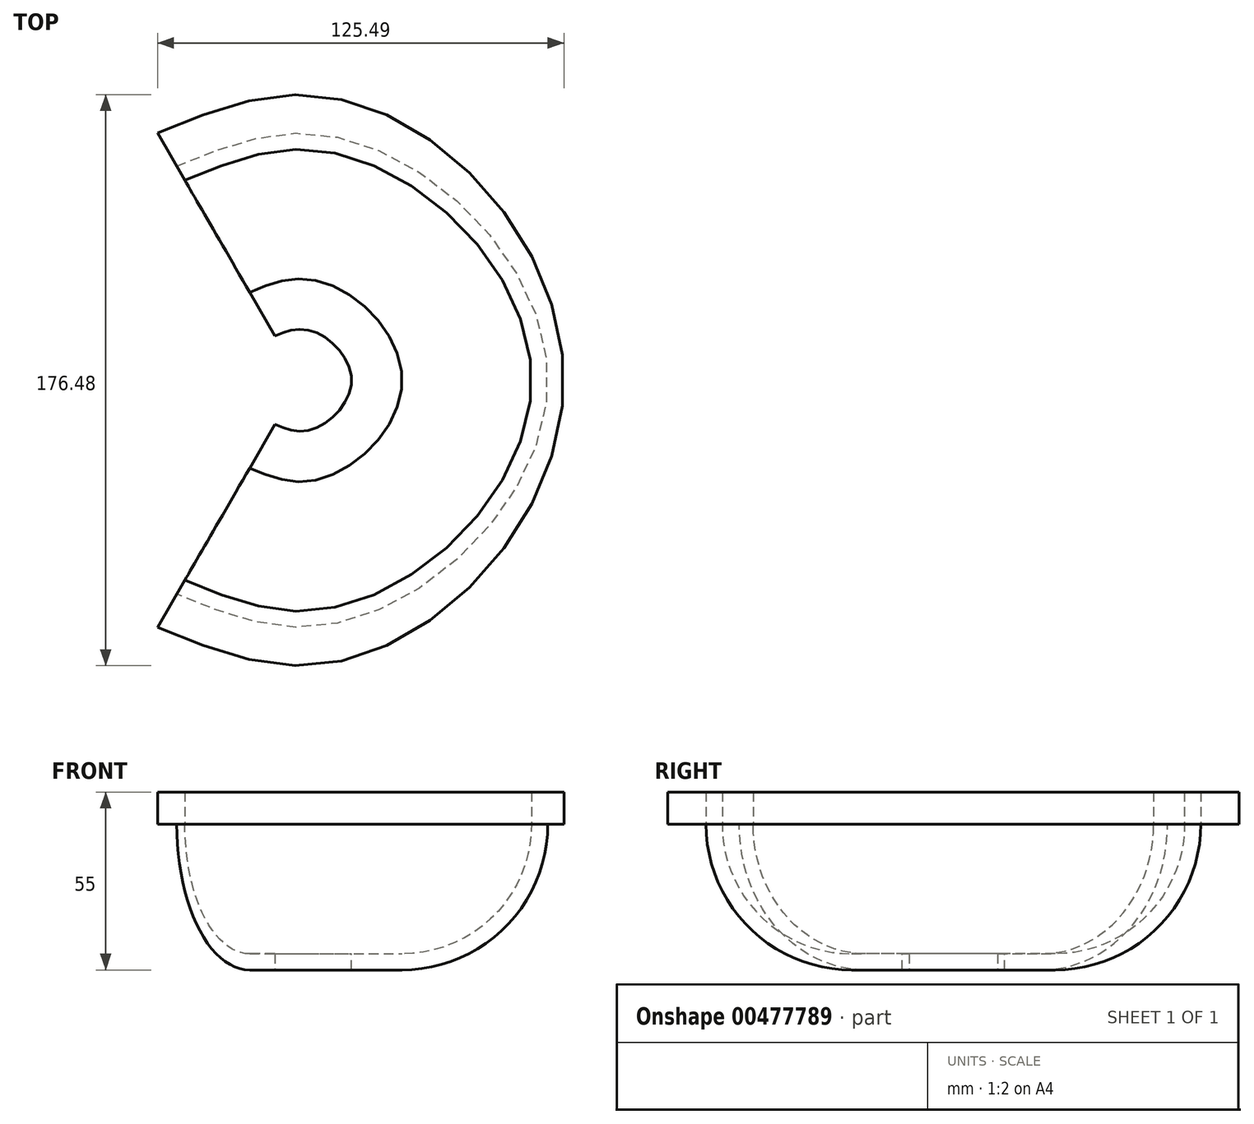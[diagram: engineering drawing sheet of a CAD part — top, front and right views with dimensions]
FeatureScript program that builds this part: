
annotation { "Feature Type Name" : "Feature", "Feature Type Description" : "" }
export const myFeature = defineFeature(function(context is Context, id is Id, definition is map)
    precondition{}
    {
        {
            var Q0;
            Q0=qCreatedBy(makeId("Front.planeOp"),FACE);
            var sketch = newSketch(context, id + "F0", { "sketchPlane" : qUnion([Q0])});
            skArc(sketch, "E0", {"start": v(31.37, 0) * mm, "mid": v(63.19, 13.18) * mm, "end": v(76.37, 45) * mm});
            skArc(sketch, "E1", {"start": v(31.37, 5) * mm, "mid": v(59.65, 16.72) * mm, "end": v(71.37, 45) * mm});
            skLineSegment(sketch, "E2.bottom", {"start": v(15.77, 5) * mm, "end": v(31.4, 5) * mm});
            skLineSegment(sketch, "E2.top", {"start": v(15.77, 0) * mm, "end": v(31.4, 0) * mm});
            skLineSegment(sketch, "E2.left", {"start": v(15.77, 5) * mm, "end": v(15.77, 0) * mm});
            skLineSegment(sketch, "E2.right", {"start": v(31.4, 5) * mm, "end": v(31.4, 0) * mm, "construction": true});
            skLineSegment(sketch, "E3.bottom", {"start": v(71.37, 55) * mm, "end": v(81.37, 55) * mm});
            skLineSegment(sketch, "E3.top", {"start": v(76.37, 45) * mm, "end": v(81.37, 45) * mm});
            skLineSegment(sketch, "E3.left", {"start": v(71.37, 55) * mm, "end": v(71.37, 45) * mm});
            skLineSegment(sketch, "E3.right", {"start": v(81.37, 55) * mm, "end": v(81.37, 45) * mm});
            skLineSegment(sketch, "E4", {"start": v(0, 0) * mm, "end": v(0, 60.2) * mm, "construction": true});
            skSolve(sketch);
        }
        {
            var Q0;
            Q0=sQuery(id+"F0.wireOp",EDGE,"E4");
            cPlane(context, id + "F1", {"entities" : qUnion([Q0]), "cplaneType" : CPlaneType.LINE_ANGLE, "offset" : 25 * mm, "angle" : 30 * degree, "width" : 150 * mm, "height" : 150 * mm});
        }
        {
            var Q0;
            Q0=qCreatedBy(id+"F1.planeOp",FACE);
            var sketch = newSketch(context, id + "F2", { "sketchPlane" : qUnion([Q0])});
            skArc(sketch, "E5", {"start": v(31.37, 0) * mm, "mid": v(63.19, 13.18) * mm, "end": v(76.37, 45) * mm});
            skArc(sketch, "E6", {"start": v(31.37, 5) * mm, "mid": v(59.65, 16.72) * mm, "end": v(71.37, 45) * mm});
            skLineSegment(sketch, "E7.bottom", {"start": v(15.77, 5) * mm, "end": v(31.4, 5) * mm});
            skLineSegment(sketch, "E7.top", {"start": v(15.77, 0) * mm, "end": v(31.4, 0) * mm});
            skLineSegment(sketch, "E7.left", {"start": v(15.77, 5) * mm, "end": v(15.77, 0) * mm});
            skLineSegment(sketch, "E7.right", {"start": v(31.4, 5) * mm, "end": v(31.4, 0) * mm, "construction": true});
            skLineSegment(sketch, "E8.bottom", {"start": v(71.37, 55) * mm, "end": v(88.24, 55) * mm});
            skLineSegment(sketch, "E8.top", {"start": v(76.37, 45) * mm, "end": v(88.24, 45) * mm});
            skLineSegment(sketch, "E8.left", {"start": v(71.37, 55) * mm, "end": v(71.37, 45) * mm});
            skLineSegment(sketch, "E8.right", {"start": v(88.24, 55) * mm, "end": v(88.24, 45) * mm});
            skLineSegment(sketch, "E9", {"start": v(0, 5) * mm, "end": v(0, 65.2) * mm, "construction": true});
            skSolve(sketch);
        }
        {
            var Q0;
            Q0=sQuery(id+"F2.wireOp",EDGE,"E9");
            cPlane(context, id + "F3", {"entities" : qUnion([Q0]), "cplaneType" : CPlaneType.LINE_ANGLE, "offset" : 25 * mm, "angle" : 150 * degree, "width" : 150 * mm, "height" : 150 * mm});
        }
        {
            var Q0;
            Q0=qCreatedBy(id+"F3.planeOp",FACE);
            var sketch = newSketch(context, id + "F4", { "sketchPlane" : qUnion([Q0])});
            skArc(sketch, "E10", {"start": v(31.37, 0) * mm, "mid": v(63.19, 13.18) * mm, "end": v(76.37, 45) * mm});
            skArc(sketch, "E11", {"start": v(31.37, 5) * mm, "mid": v(59.65, 16.72) * mm, "end": v(71.37, 45) * mm});
            skLineSegment(sketch, "E12.bottom", {"start": v(15.77, 5) * mm, "end": v(31.4, 5) * mm});
            skLineSegment(sketch, "E12.top", {"start": v(15.77, 0) * mm, "end": v(31.4, 0) * mm});
            skLineSegment(sketch, "E12.left", {"start": v(15.77, 5) * mm, "end": v(15.77, 0) * mm});
            skLineSegment(sketch, "E12.right", {"start": v(31.4, 5) * mm, "end": v(31.4, 0) * mm, "construction": true});
            skLineSegment(sketch, "E13.bottom", {"start": v(71.37, 55) * mm, "end": v(88.24, 55) * mm});
            skLineSegment(sketch, "E13.top", {"start": v(76.37, 45) * mm, "end": v(88.24, 45) * mm});
            skLineSegment(sketch, "E13.left", {"start": v(71.37, 55) * mm, "end": v(71.37, 45) * mm});
            skLineSegment(sketch, "E13.right", {"start": v(88.24, 55) * mm, "end": v(88.24, 45) * mm});
            skLineSegment(sketch, "E14", {"start": v(0, 0) * mm, "end": v(0, 60.2) * mm, "construction": true});
            skSolve(sketch);
        }
        {
            var Q0;
            Q0=qCreatedBy(makeId("Right.planeOp"),FACE);
            var sketch = newSketch(context, id + "F5", { "sketchPlane" : qUnion([Q0])});
            skArc(sketch, "E15", {"start": v(31.37, 0) * mm, "mid": v(63.19, 13.18) * mm, "end": v(76.37, 45) * mm});
            skArc(sketch, "E16", {"start": v(31.37, 5) * mm, "mid": v(59.65, 16.72) * mm, "end": v(71.37, 45) * mm});
            skLineSegment(sketch, "E17.bottom", {"start": v(15.77, 5) * mm, "end": v(31.4, 5) * mm});
            skLineSegment(sketch, "E17.top", {"start": v(15.77, 0) * mm, "end": v(31.4, 0) * mm});
            skLineSegment(sketch, "E17.left", {"start": v(15.77, 5) * mm, "end": v(15.77, 0) * mm});
            skLineSegment(sketch, "E17.right", {"start": v(31.4, 5) * mm, "end": v(31.4, 0) * mm, "construction": true});
            skLineSegment(sketch, "E18.bottom", {"start": v(71.37, 55) * mm, "end": v(88.24, 55) * mm});
            skLineSegment(sketch, "E18.top", {"start": v(76.37, 45) * mm, "end": v(88.24, 45) * mm});
            skLineSegment(sketch, "E18.left", {"start": v(71.37, 55) * mm, "end": v(71.37, 45) * mm});
            skLineSegment(sketch, "E18.right", {"start": v(88.24, 55) * mm, "end": v(88.24, 45) * mm});
            skLineSegment(sketch, "E19", {"start": v(0, 0) * mm, "end": v(0, 60.2) * mm, "construction": true});
            skSolve(sketch);
        }
        {
            var Q0;
            Q0=sQuery(id+"F5.wireOp",EDGE,"E19");
            cPlane(context, id + "F6", {"entities" : qUnion([Q0]), "cplaneType" : CPlaneType.LINE_ANGLE, "offset" : 25 * mm, "angle" : 0 * degree, "width" : 150 * mm, "height" : 150 * mm});
        }
        {
            var Q0;
            Q0=qCreatedBy(id+"F6.planeOp",FACE);
            var sketch = newSketch(context, id + "F7", { "sketchPlane" : qUnion([Q0])});
            skArc(sketch, "E20", {"start": v(31.37, 0) * mm, "mid": v(63.19, 13.18) * mm, "end": v(76.37, 45) * mm});
            skArc(sketch, "E21", {"start": v(31.37, 5) * mm, "mid": v(59.65, 16.72) * mm, "end": v(71.37, 45) * mm});
            skLineSegment(sketch, "E22.bottom", {"start": v(15.77, 5) * mm, "end": v(31.4, 5) * mm});
            skLineSegment(sketch, "E22.top", {"start": v(15.77, 0) * mm, "end": v(31.4, 0) * mm});
            skLineSegment(sketch, "E22.left", {"start": v(15.77, 5) * mm, "end": v(15.77, 0) * mm});
            skLineSegment(sketch, "E22.right", {"start": v(31.4, 5) * mm, "end": v(31.4, 0) * mm, "construction": true});
            skLineSegment(sketch, "E23.bottom", {"start": v(71.37, 55) * mm, "end": v(88.24, 55) * mm});
            skLineSegment(sketch, "E23.top", {"start": v(76.37, 45) * mm, "end": v(88.24, 45) * mm});
            skLineSegment(sketch, "E23.left", {"start": v(71.37, 55) * mm, "end": v(71.37, 45) * mm});
            skLineSegment(sketch, "E23.right", {"start": v(88.24, 55) * mm, "end": v(88.24, 45) * mm});
            skLineSegment(sketch, "E24", {"start": v(0, 0) * mm, "end": v(0, 60.2) * mm, "construction": true});
            skSolve(sketch);
        }
        {
            var Q0;
            Q0=sQuery(id+"F7.wireOp",EDGE,"E24");
            cPlane(context, id + "F8", {"entities" : qUnion([Q0]), "cplaneType" : CPlaneType.LINE_ANGLE, "offset" : 25 * mm, "angle" : 180 * degree, "oppositeDirection" : true, "width" : 150 * mm, "height" : 150 * mm});
        }
        {
            var Q0;
            Q0=qCreatedBy(id+"F8.planeOp",FACE);
            var sketch = newSketch(context, id + "F9", { "sketchPlane" : qUnion([Q0])});
            skArc(sketch, "E25", {"start": v(31.37, 0) * mm, "mid": v(63.19, 13.18) * mm, "end": v(76.37, 45) * mm});
            skArc(sketch, "E26", {"start": v(31.37, 5) * mm, "mid": v(59.65, 16.72) * mm, "end": v(71.37, 45) * mm});
            skLineSegment(sketch, "E27.bottom", {"start": v(15.77, 5) * mm, "end": v(31.4, 5) * mm});
            skLineSegment(sketch, "E27.top", {"start": v(15.77, 0) * mm, "end": v(31.4, 0) * mm});
            skLineSegment(sketch, "E27.left", {"start": v(15.77, 5) * mm, "end": v(15.77, 0) * mm});
            skLineSegment(sketch, "E27.right", {"start": v(31.4, 5) * mm, "end": v(31.4, 0) * mm, "construction": true});
            skLineSegment(sketch, "E28.bottom", {"start": v(71.37, 55) * mm, "end": v(88.24, 55) * mm});
            skLineSegment(sketch, "E28.top", {"start": v(76.37, 45) * mm, "end": v(88.24, 45) * mm});
            skLineSegment(sketch, "E28.left", {"start": v(71.37, 55) * mm, "end": v(71.37, 45) * mm});
            skLineSegment(sketch, "E28.right", {"start": v(88.24, 55) * mm, "end": v(88.24, 45) * mm});
            skLineSegment(sketch, "E29", {"start": v(0, 0) * mm, "end": v(0, 60.2) * mm, "construction": true});
            skSolve(sketch);
        }
        {
            var Q0;
            {var subQ1=sQuery(id+"F2.wireOp",EDGE,"E5");Q0=makeQuery(id+"F2.imprint","IMPRINT",FACE,{"disambiguationData":[TD([[makeQuery(id+"F2.imprint","IMPRINT",EDGE,{"derivedFrom":subQ1}),1.0]])]});}
            var Q1;
            {var subQ1=sQuery(id+"F5.wireOp",EDGE,"E15");Q1=makeQuery(id+"F5.imprint","IMPRINT",FACE,{"disambiguationData":[TD([[makeQuery(id+"F5.imprint","IMPRINT",EDGE,{"derivedFrom":subQ1}),1.0]])]});}
            var Q2;
            {var subQ1=sQuery(id+"F0.wireOp",EDGE,"E0");Q2=makeQuery(id+"F0.imprint","IMPRINT",FACE,{"disambiguationData":[TD([[makeQuery(id+"F0.imprint","IMPRINT",EDGE,{"derivedFrom":subQ1}),1.0]])]});}
            var Q3;
            {var subQ1=sQuery(id+"F9.wireOp",EDGE,"E25");Q3=makeQuery(id+"F9.imprint","IMPRINT",FACE,{"disambiguationData":[TD([[makeQuery(id+"F9.imprint","IMPRINT",EDGE,{"derivedFrom":subQ1}),1.0]])]});}
            var Q4;
            {var subQ1=sQuery(id+"F4.wireOp",EDGE,"E10");Q4=makeQuery(id+"F4.imprint","IMPRINT",FACE,{"disambiguationData":[TD([[makeQuery(id+"F4.imprint","IMPRINT",EDGE,{"derivedFrom":subQ1}),1.0]])]});}
            loft(context, id + "F10", {"sheetProfilesArray" : [{ "sheetProfileEntities" : qUnion([Q0]) }, { "sheetProfileEntities" : qUnion([Q1]) }, { "sheetProfileEntities" : qUnion([Q2]) }, { "sheetProfileEntities" : qUnion([Q3]) }, { "sheetProfileEntities" : qUnion([Q4]) }]});
        }
    });
